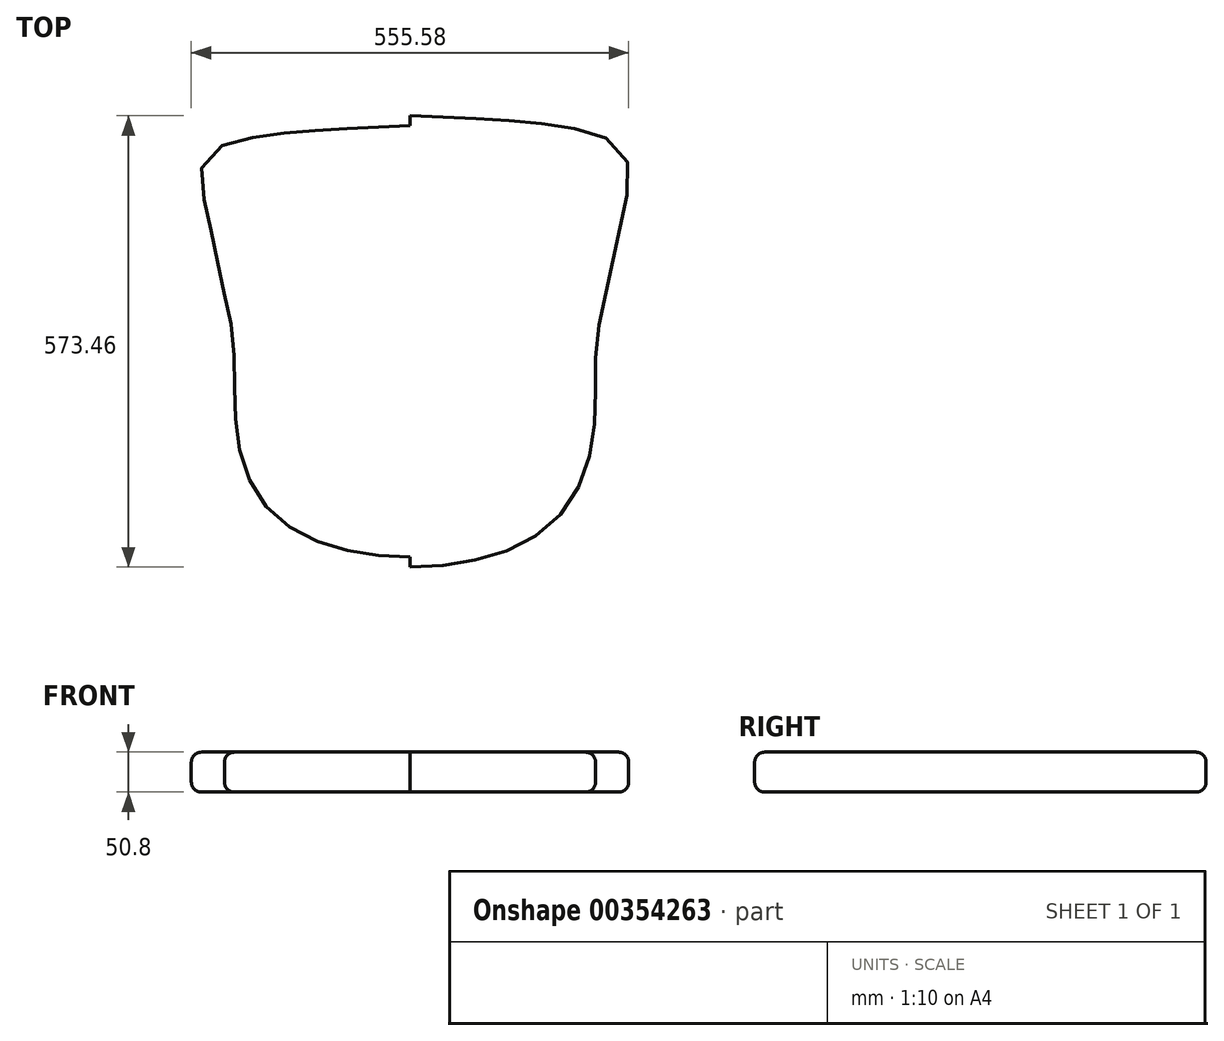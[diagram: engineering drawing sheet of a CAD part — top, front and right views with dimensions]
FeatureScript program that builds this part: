
annotation { "Feature Type Name" : "Feature", "Feature Type Description" : "" }
export const myFeature = defineFeature(function(context is Context, id is Id, definition is map)
    precondition{}
    {
        {
            var Q0;
            Q0=qCreatedBy(makeId("Top.planeOp"),FACE);
            var sketch = newSketch(context, id + "F0", { "sketchPlane" : qUnion([Q0])});
            skFitSpline(sketch, "E0", {"points": [v(0, 317.26) * mm, v(-277.44, 249.9) * mm, v(-262.44, 155.99) * mm, v(-246.17, 78.36) * mm, v(-235.65, 0) * mm, v(0, -256.2) * mm], "startDerivative": vector(-2607.12, -88.38) * mm, "endDerivative": vector(2580.18, -48.7) * mm});
            skLineSegment(sketch, "E1", {"start": v(0, 67.9) * mm, "end": v(0, -44.25) * mm, "construction": true});
            skFitSpline(sketch, "E2.MirrorCS", {"points": [v(0, 317.26) * mm, v(277.44, 249.9) * mm, v(262.44, 155.99) * mm, v(246.17, 78.36) * mm, v(235.65, 0) * mm, v(0, -256.2) * mm], "startDerivative": vector(2607.12, -88.38) * mm, "endDerivative": vector(-2580.18, -48.7) * mm});
            skSolve(sketch);
        }
        {
            var Q0;
            Q0 = qSketchRegion(id + "F0", true);
            extrude(context, id + "F1", {"entities" : qUnion([Q0]), "endBound" : BoundingType.SYMMETRIC, "depth" : 50.8 * mm});
        }
        {
            var Q0;
            Q0=makeQuery(id+"F1.opExtrude","CAP_EDGE",EDGE,{"disambiguationData":[OSD([sQuery(id+"F0.wireOp",EDGE,"E0")])],"isStart":false});
            var Q1;
            Q1=makeQuery(id+"F1.opExtrude","CAP_EDGE",EDGE,{"disambiguationData":[OSD([sQuery(id+"F0.wireOp",EDGE,"E0")])],"isStart":true});
            var Q2;
            Q2=makeQuery(id+"F1.opExtrude","CAP_EDGE",EDGE,{"disambiguationData":[OSD([sQuery(id+"F0.wireOp",EDGE,"E2.MirrorCS")])],"isStart":true});
            var Q3;
            Q3=makeQuery(id+"F1.opExtrude","CAP_EDGE",EDGE,{"disambiguationData":[OSD([sQuery(id+"F0.wireOp",EDGE,"E2.MirrorCS")])],"isStart":false});
            fillet(context, id + "F2", {"entities" : qUnion([Q0, Q1, Q2, Q3]), "radius" : 12.7 * mm, "tangentPropagation" : true, "allowEdgeOverflow" : false});
        }
    });
